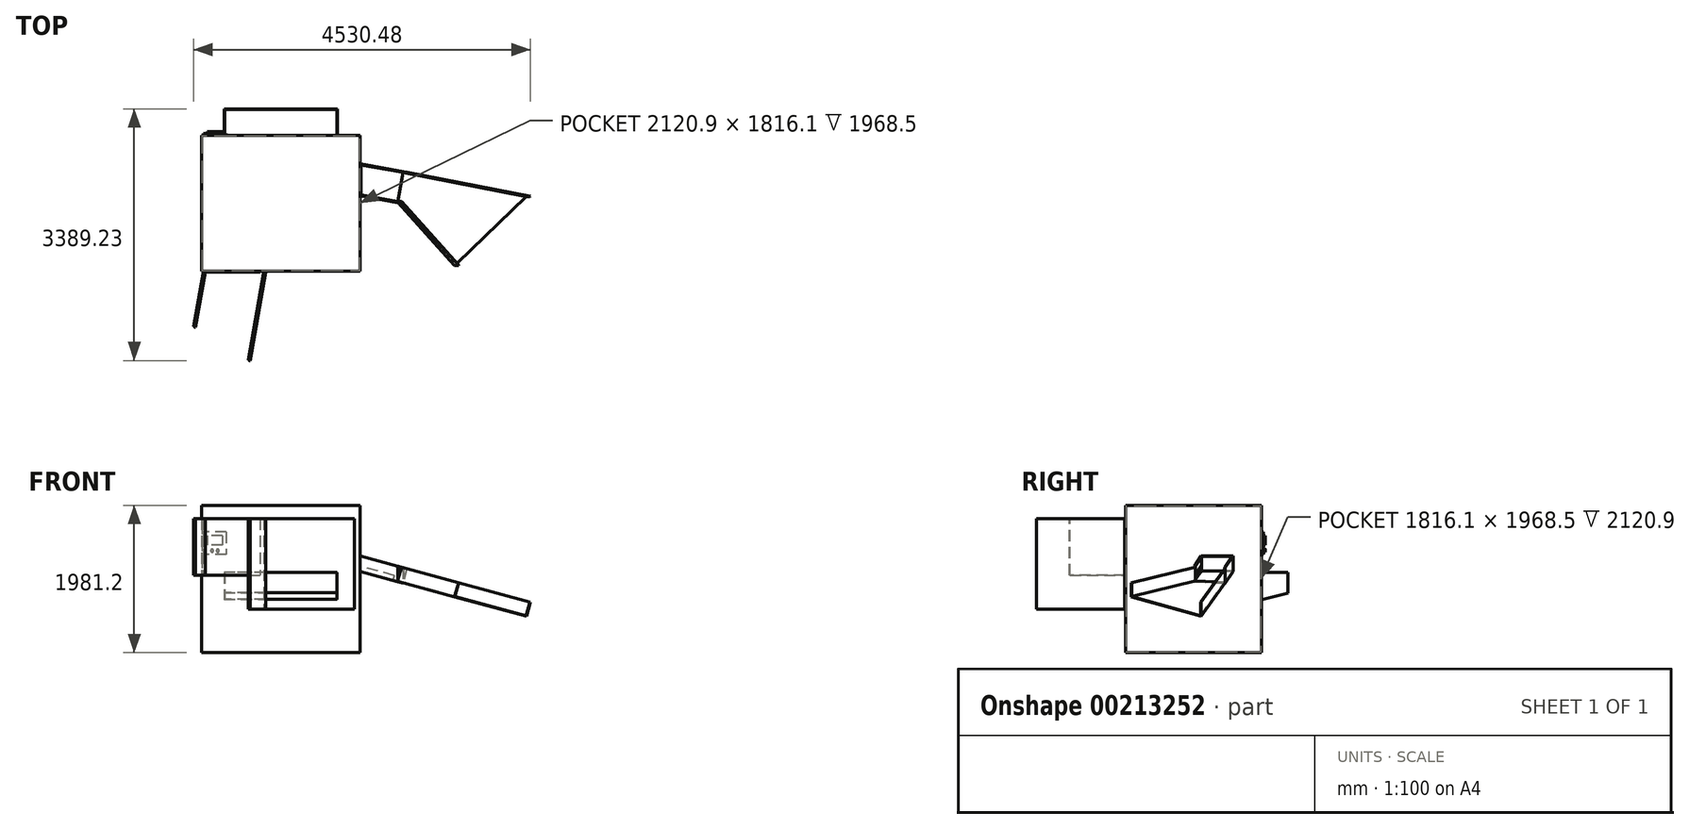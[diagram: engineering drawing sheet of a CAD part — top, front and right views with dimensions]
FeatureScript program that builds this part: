
annotation { "Feature Type Name" : "Feature", "Feature Type Description" : "" }
export const myFeature = defineFeature(function(context is Context, id is Id, definition is map)
    precondition{}
    {
        {
            var Q0;
            Q0=qCreatedBy(makeId("Top.planeOp"),FACE);
            var sketch = newSketch(context, id + "F0", { "sketchPlane" : qUnion([Q0])});
            skLineSegment(sketch, "E0", {"start": v(0, 1828.8) * mm, "end": v(304.8, 1828.8) * mm});
            skLineSegment(sketch, "E1", {"start": v(304.8, 1828.8) * mm, "end": v(304.8, 2184.4) * mm});
            skLineSegment(sketch, "E2", {"start": v(304.8, 2184.4) * mm, "end": v(1828.8, 2184.4) * mm});
            skLineSegment(sketch, "E3", {"start": v(1828.8, 2184.4) * mm, "end": v(1828.8, 1828.8) * mm});
            skLineSegment(sketch, "E4", {"start": v(1828.8, 1828.8) * mm, "end": v(2133.6, 1828.8) * mm});
            skLineSegment(sketch, "E5", {"start": v(2133.6, 1828.8) * mm, "end": v(2133.6, 0) * mm});
            skLineSegment(sketch, "E6", {"start": v(2133.6, 0) * mm, "end": v(0, 0) * mm});
            skLineSegment(sketch, "E7", {"start": v(0, 0) * mm, "end": v(0, 1828.8) * mm});
            skLineSegment(sketch, "E8", {"start": v(2133.6, 1828.8) * mm, "end": v(2133.6, 1447.8) * mm});
            skLineSegment(sketch, "E9", {"start": v(2133.6, 1447.8) * mm, "end": v(2717.8, 1341.28) * mm});
            skLineSegment(sketch, "E10", {"start": v(2717.8, 1341.28) * mm, "end": v(2641.6, 923.37) * mm});
            skLineSegment(sketch, "E11", {"start": v(2641.6, 923.37) * mm, "end": v(2133.6, 1016) * mm});
            skLineSegment(sketch, "E12", {"start": v(2133.6, 1016) * mm, "end": v(2133.6, 1447.8) * mm});
            skSolve(sketch);
        }
        {
            var Q0;
            Q0=makeQuery(id+"F0.imprint","IMPRINT",FACE,{"disambiguationData":[TD([[makeQuery(id+"F0.imprint","IMPRINT",EDGE,{"derivedFrom":sQuery(id+"F0.wireOp",EDGE,"E0")}),-1.0]])]});
            var Q1;
            Q1=makeQuery(id+"F0.imprint","IMPRINT",FACE,{"disambiguationData":[TD([[makeQuery(id+"F0.imprint","IMPRINT",EDGE,{"derivedFrom":sQuery(id+"F0.wireOp",EDGE,"E9")}),-1.0]])]});
            extrude(context, id + "F1", {"entities" : qUnion([Q0, Q1]), "depth" : 1981.2 * mm});
        }
        {
            var Q0;
            Q0=qCreatedBy(makeId("Front.planeOp"),FACE);
            var sketch = newSketch(context, id + "F2", { "sketchPlane" : qUnion([Q0])});
            skLineSegment(sketch, "E13", {"start": v(2133.6, 0) * mm, "end": v(2133.6, 1092.2) * mm});
            skLineSegment(sketch, "E14", {"start": v(2133.6, 1092.2) * mm, "end": v(2717.8, 932.33) * mm});
            skLineSegment(sketch, "E15", {"start": v(2717.8, 932.33) * mm, "end": v(2717.8, 0) * mm});
            skLineSegment(sketch, "E16", {"start": v(2717.8, 0) * mm, "end": v(2133.6, 0) * mm});
            skLineSegment(sketch, "E17", {"start": v(2133.6, 1981.2) * mm, "end": v(2717.8, 1981.2) * mm});
            skLineSegment(sketch, "E18", {"start": v(2717.8, 1981.2) * mm, "end": v(2717.8, 1143) * mm});
            skLineSegment(sketch, "E19", {"start": v(2717.8, 1143) * mm, "end": v(2133.6, 1302.87) * mm});
            skLineSegment(sketch, "E20", {"start": v(2133.6, 1302.87) * mm, "end": v(2133.6, 1981.2) * mm});
            skSolve(sketch);
        }
        {
            var Q0;
            Q0=makeQuery(id+"F2.imprint","IMPRINT",FACE,{"disambiguationData":[TD([[makeQuery(id+"F2.imprint","IMPRINT",EDGE,{"derivedFrom":sQuery(id+"F2.wireOp",EDGE,"E17")}),-1.0]])]});
            var Q1;
            Q1=makeQuery(id+"F2.imprint","IMPRINT",FACE,{"disambiguationData":[TD([[makeQuery(id+"F2.imprint","IMPRINT",EDGE,{"derivedFrom":sQuery(id+"F2.wireOp",EDGE,"E13")}),-1.0]])]});
            extrude(context, id + "F3", {"entities" : qUnion([Q0, Q1]), "operationType" : NewBodyOperationType.REMOVE, "endBound" : BoundingType.THROUGH_ALL, "oppositeDirection" : true, "depth" : 25.4 * mm});
        }
        {
            var Q0;
            Q0=makeQuery(id+"F1.opExtrude","SWEPT_FACE",FACE,{"disambiguationData":[OSD([sQuery(id+"F0.wireOp",EDGE,"E7")])]});
            var sketch = newSketch(context, id + "F4", { "sketchPlane" : qUnion([Q0])});
            skLineSegment(sketch, "E21", {"start": v(-1828.8, 0) * mm, "end": v(-2184.4, 0) * mm});
            skLineSegment(sketch, "E22", {"start": v(-2184.4, 0) * mm, "end": v(-2184.4, 800.1) * mm});
            skLineSegment(sketch, "E23", {"start": v(-2184.4, 800.1) * mm, "end": v(-1828.8, 711.2) * mm});
            skLineSegment(sketch, "E24", {"start": v(-1828.8, 711.2) * mm, "end": v(-1828.8, 0) * mm});
            skLineSegment(sketch, "E25", {"start": v(-1828.8, 1981.2) * mm, "end": v(-2184.4, 1981.2) * mm});
            skLineSegment(sketch, "E26", {"start": v(-2184.4, 1981.2) * mm, "end": v(-2184.4, 1079.5) * mm});
            skLineSegment(sketch, "E27", {"start": v(-2184.4, 1079.5) * mm, "end": v(-1828.8, 1079.5) * mm});
            skLineSegment(sketch, "E28", {"start": v(-1828.8, 1079.5) * mm, "end": v(-1828.8, 1981.2) * mm});
            skSolve(sketch);
        }
        {
            var Q0;
            Q0=makeQuery(id+"F4.imprint","IMPRINT",FACE,{"disambiguationData":[TD([[makeQuery(id+"F4.imprint","IMPRINT",EDGE,{"derivedFrom":sQuery(id+"F4.wireOp",EDGE,"E25")}),1.0]])]});
            var Q1;
            Q1=makeQuery(id+"F4.imprint","IMPRINT",FACE,{"disambiguationData":[TD([[makeQuery(id+"F4.imprint","IMPRINT",EDGE,{"derivedFrom":sQuery(id+"F4.wireOp",EDGE,"E21")}),-1.0]])]});
            extrude(context, id + "F5", {"entities" : qUnion([Q0, Q1]), "operationType" : NewBodyOperationType.REMOVE, "endBound" : BoundingType.THROUGH_ALL, "oppositeDirection" : true, "depth" : 25.4 * mm});
        }
        {
            var Q0;
            Q0=makeQuery(id+"F5.boolean.opBoolean","COPY",FACE,{"derivedFrom":makeQuery(id+"F5.opExtrude","SWEPT_FACE",FACE,{"disambiguationData":[OSD([sQuery(id+"F4.wireOp",EDGE,"E27")])]})});
            shell(context, id + "F6", {"entities" : qUnion([Q0]), "thickness" : 6.35 * mm});
        }
        {
            var Q0;
            Q0=makeQuery(id+"F3.boolean.opBoolean","COPY",FACE,{"derivedFrom":makeQuery(id+"F3.opExtrude","SWEPT_FACE",FACE,{"disambiguationData":[OSD([sQuery(id+"F2.wireOp",EDGE,"E19")])]})});
            var sketch = newSketch(context, id + "F7", { "sketchPlane" : qUnion([Q0])});
            skLineSegment(sketch, "E29.0", {"start": v(2230.56, 938.05) * mm, "end": v(2304.85, 1331) * mm});
            skLineSegment(sketch, "E29.1", {"start": v(1726.74, 1026.66) * mm, "end": v(2230.56, 938.05) * mm});
            skLineSegment(sketch, "E29.2", {"start": v(1726.74, 1432.67) * mm, "end": v(1726.74, 1026.66) * mm});
            skLineSegment(sketch, "E29.3", {"start": v(2304.85, 1331) * mm, "end": v(1726.74, 1432.67) * mm});
            skSolve(sketch);
        }
        {
            var Q0;
            Q0=makeQuery(id+"F7.imprint","IMPRINT",FACE,{"disambiguationData":[TD([[makeQuery(id+"F7.imprint","IMPRINT",EDGE,{"derivedFrom":sQuery(id+"F7.wireOp",EDGE,"E29.0")}),1.0]])]});
            extrude(context, id + "F8", {"entities" : qUnion([Q0]), "operationType" : NewBodyOperationType.REMOVE, "oppositeDirection" : true, "depth" : 196.85 * mm});
        }
        {
            var Q0;
            Q0=makeQuery(id+"F1.opExtrude","SWEPT_FACE",FACE,{"disambiguationData":[OSD([sQuery(id+"F0.wireOp",EDGE,"E10")])]});
            var sketch = newSketch(context, id + "F9", { "sketchPlane" : qUnion([Q0])});
            skLineSegment(sketch, "E30", {"start": v(1794.36, 1143.62) * mm, "end": v(1794.36, 945.67) * mm});
            skLineSegment(sketch, "E31", {"start": v(1794.36, 945.67) * mm, "end": v(1394.93, 965.27) * mm});
            skLineSegment(sketch, "E32", {"start": v(1394.93, 965.27) * mm, "end": v(1394.93, 1163.23) * mm});
            skLineSegment(sketch, "E33", {"start": v(1794.36, 1143.62) * mm, "end": v(1798.95, 1186.6) * mm});
            skLineSegment(sketch, "E34", {"start": v(1798.95, 1186.6) * mm, "end": v(1379.63, 1213.91) * mm});
            skLineSegment(sketch, "E35", {"start": v(1379.63, 1213.91) * mm, "end": v(1394.93, 1163.23) * mm});
            skSolve(sketch);
        }
        {
            var Q0;
            Q0=makeQuery(id+"F9.imprint","IMPRINT",FACE,{"disambiguationData":[TD([[makeQuery(id+"F9.imprint","IMPRINT",EDGE,{"derivedFrom":sQuery(id+"F9.wireOp",EDGE,"E30")}),-1.0]])]});
            var Q1;
            {var subQ0=sQuery(id+"F9.wireOp",EDGE,"E33");Q1=makeQuery(id+"F9.imprint","IMPRINT",FACE,{"disambiguationData":[TD([[makeQuery(id+"F9.imprint","IMPRINT",EDGE,{"derivedFrom":subQ0}),1.0]])]});}
            extrude(context, id + "F10", {"entities" : qUnion([Q0, Q1]), "operationType" : NewBodyOperationType.REMOVE, "oppositeDirection" : true, "depth" : 19.05 * mm});
        }
        {
            var Q0;
            Q0=makeQuery(id+"F1.opExtrude","SWEPT_FACE",FACE,{"disambiguationData":[OSD([sQuery(id+"F0.wireOp",EDGE,"E6")])]});
            var sketch = newSketch(context, id + "F11", { "sketchPlane" : qUnion([Q0])});
            skLineSegment(sketch, "E36.bottom", {"start": v(838.2, 1803.4) * mm, "end": v(2057.4, 1803.4) * mm});
            skLineSegment(sketch, "E36.top", {"start": v(838.2, 584.2) * mm, "end": v(2057.4, 584.2) * mm});
            skLineSegment(sketch, "E36.left", {"start": v(838.2, 1803.4) * mm, "end": v(838.2, 584.2) * mm});
            skLineSegment(sketch, "E36.right", {"start": v(2057.4, 1803.4) * mm, "end": v(2057.4, 584.2) * mm});
            skLineSegment(sketch, "E37.bottom", {"start": v(25.4, 1803.4) * mm, "end": v(787.4, 1803.4) * mm});
            skLineSegment(sketch, "E37.top", {"start": v(25.4, 1041.4) * mm, "end": v(787.4, 1041.4) * mm});
            skLineSegment(sketch, "E37.left", {"start": v(25.4, 1803.4) * mm, "end": v(25.4, 1041.4) * mm});
            skLineSegment(sketch, "E37.right", {"start": v(787.4, 1803.4) * mm, "end": v(787.4, 1041.4) * mm});
            skSolve(sketch);
        }
        {
            var Q0;
            Q0=makeQuery(id+"F11.imprint","IMPRINT",FACE,{"disambiguationData":[TD([[makeQuery(id+"F11.imprint","IMPRINT",EDGE,{"derivedFrom":sQuery(id+"F11.wireOp",EDGE,"E37.bottom")}),-1.0]])]});
            var Q1;
            Q1=makeQuery(id+"F11.imprint","IMPRINT",FACE,{"disambiguationData":[TD([[makeQuery(id+"F11.imprint","IMPRINT",EDGE,{"derivedFrom":sQuery(id+"F11.wireOp",EDGE,"E36.bottom")}),-1.0]])]});
            extrude(context, id + "F12", {"entities" : qUnion([Q0, Q1]), "operationType" : NewBodyOperationType.ADD, "depth" : 12.7 * mm});
        }
        {
            var Q0;
            Q0=makeQuery(id+"F12.opExtrude","SWEPT_FACE",FACE,{"disambiguationData":[OSD([sQuery(id+"F11.wireOp",EDGE,"E36.bottom")])]});
            var sketch = newSketch(context, id + "F13", { "sketchPlane" : qUnion([Q0])});
            skCircle(sketch, "E38", {"center": v(838.2, 0) * mm, "radius": 1219.2 * mm});
            skLineSegment(sketch, "E39", {"start": v(838.2, 0) * mm, "end": v(626.49, -1200.68) * mm});
            skLineSegment(sketch, "E40", {"start": v(626.49, -1200.68) * mm, "end": v(651.5, -1205.09) * mm});
            skLineSegment(sketch, "E41", {"start": v(651.5, -1205.09) * mm, "end": v(863.21, -4.41) * mm});
            skLineSegment(sketch, "E42", {"start": v(863.21, -4.41) * mm, "end": v(838.2, 0) * mm});
            skSolve(sketch);
        }
        {
            var Q0;
            {var subQ7=sQuery(id+"F13.wireOp",EDGE,"E39");Q0=makeQuery(id+"F13.imprint","IMPRINT",FACE,{"disambiguationData":[TD([[makeQuery(id+"F13.imprint","IMPRINT",EDGE,{"derivedFrom":subQ7}),1.0]])]});}
            var Q1;
            Q1=makeQuery(id+"F12.opExtrude","SWEPT_FACE",FACE,{"disambiguationData":[OSD([sQuery(id+"F11.wireOp",EDGE,"E36.top")])]});
            extrude(context, id + "F14", {"entities" : qUnion([Q0]), "operationType" : NewBodyOperationType.ADD, "endBound" : BoundingType.UP_TO_SURFACE, "oppositeDirection" : true, "endBoundEntityFace" : qUnion([Q1]), "depth" : 25.4 * mm});
        }
        {
            var Q0;
            Q0=makeQuery(id+"F12.opExtrude","CAP_FACE",FACE,{"disambiguationData":[OSD([sQuery(id+"F11.wireOp",EDGE,"E36.bottom"),sQuery(id+"F11.wireOp",EDGE,"E36.top"),sQuery(id+"F11.wireOp",EDGE,"E36.left"),sQuery(id+"F11.wireOp",EDGE,"E36.right")])],"isStart":false});
            extrude(context, id + "F15", {"entities" : qUnion([Q0]), "operationType" : NewBodyOperationType.REMOVE, "oppositeDirection" : true, "depth" : 25.4 * mm});
        }
        {
            var Q0;
            Q0=makeQuery(id+"F12.opExtrude","SWEPT_FACE",FACE,{"disambiguationData":[OSD([sQuery(id+"F11.wireOp",EDGE,"E37.bottom")])]});
            var sketch = newSketch(context, id + "F16", { "sketchPlane" : qUnion([Q0])});
            skCircle(sketch, "E43", {"center": v(25.4, 0) * mm, "radius": 762 * mm});
            skLineSegment(sketch, "E44", {"start": v(25.4, 0) * mm, "end": v(-106.92, -750.42) * mm});
            skLineSegment(sketch, "E45", {"start": v(-106.92, -750.42) * mm, "end": v(-81.9, -754.83) * mm});
            skLineSegment(sketch, "E46", {"start": v(-81.9, -754.83) * mm, "end": v(50.41, -4.41) * mm});
            skLineSegment(sketch, "E47", {"start": v(50.41, -4.41) * mm, "end": v(25.4, 0) * mm});
            skSolve(sketch);
        }
        {
            var Q0;
            {var subQ2=sQuery(id+"F16.wireOp",EDGE,"E44");Q0=makeQuery(id+"F16.imprint","IMPRINT",FACE,{"disambiguationData":[TD([[makeQuery(id+"F16.imprint","IMPRINT",EDGE,{"derivedFrom":subQ2}),1.0]])]});}
            var Q1;
            Q1=makeQuery(id+"F12.opExtrude","SWEPT_FACE",FACE,{"disambiguationData":[OSD([sQuery(id+"F11.wireOp",EDGE,"E37.top")])]});
            extrude(context, id + "F17", {"entities" : qUnion([Q0]), "operationType" : NewBodyOperationType.ADD, "endBound" : BoundingType.UP_TO_SURFACE, "oppositeDirection" : true, "endBoundEntityFace" : qUnion([Q1]), "depth" : 25.4 * mm});
        }
        {
            var Q0;
            Q0=makeQuery(id+"F5.boolean.opBoolean","MERGE",FACE,{"derivedFrom":[makeQuery(id+"F1.opExtrude","SWEPT_FACE",FACE,{"disambiguationData":[OSD([sQuery(id+"F0.wireOp",EDGE,"E0")])]}),makeQuery(id+"F1.opExtrude","SWEPT_FACE",FACE,{"disambiguationData":[OSD([sQuery(id+"F0.wireOp",EDGE,"E4")])]}),makeQuery(id+"F5.opExtrude","SWEPT_FACE",FACE,{"disambiguationData":[OSD([sQuery(id+"F4.wireOp",EDGE,"E24")])]}),makeQuery(id+"F5.opExtrude","SWEPT_FACE",FACE,{"disambiguationData":[OSD([sQuery(id+"F4.wireOp",EDGE,"E28")])]})]});
            var sketch = newSketch(context, id + "F18", { "sketchPlane" : qUnion([Q0])});
            skLineSegment(sketch, "E48.bottom", {"start": v(-330.2, 1625.6) * mm, "end": v(-25.4, 1625.6) * mm});
            skLineSegment(sketch, "E48.top", {"start": v(-330.2, 1320.8) * mm, "end": v(-25.4, 1320.8) * mm});
            skLineSegment(sketch, "E48.left", {"start": v(-330.2, 1625.6) * mm, "end": v(-330.2, 1320.8) * mm});
            skLineSegment(sketch, "E48.right", {"start": v(-25.4, 1625.6) * mm, "end": v(-25.4, 1320.8) * mm});
            skSolve(sketch);
        }
        {
            var Q0;
            Q0=makeQuery(id+"F18.imprint","IMPRINT",FACE,{"disambiguationData":[TD([[makeQuery(id+"F18.imprint","IMPRINT",EDGE,{"derivedFrom":sQuery(id+"F18.wireOp",EDGE,"E48.bottom")}),-1.0]])]});
            extrude(context, id + "F19", {"entities" : qUnion([Q0]), "operationType" : NewBodyOperationType.ADD, "depth" : 25.4 * mm});
        }
        {
            var Q0;
            Q0=makeQuery(id+"F19.opExtrude","CAP_FACE",FACE,{"disambiguationData":[OSD([sQuery(id+"F18.wireOp",EDGE,"E48.bottom"),sQuery(id+"F18.wireOp",EDGE,"E48.top"),sQuery(id+"F18.wireOp",EDGE,"E48.left"),sQuery(id+"F18.wireOp",EDGE,"E48.right")])],"isStart":false});
            var sketch = newSketch(context, id + "F20", { "sketchPlane" : qUnion([Q0])});
            skLineSegment(sketch, "E49.bottom", {"start": v(-279.4, 1574.8) * mm, "end": v(-76.2, 1574.8) * mm});
            skLineSegment(sketch, "E49.top", {"start": v(-279.4, 1447.8) * mm, "end": v(-76.2, 1447.8) * mm});
            skLineSegment(sketch, "E49.left", {"start": v(-279.4, 1574.8) * mm, "end": v(-279.4, 1447.8) * mm});
            skLineSegment(sketch, "E49.right", {"start": v(-76.2, 1574.8) * mm, "end": v(-76.2, 1447.8) * mm});
            skCircle(sketch, "E50", {"center": v(-215.9, 1371.6) * mm, "radius": 19.05 * mm});
            skCircle(sketch, "E51", {"center": v(-139.7, 1371.6) * mm, "radius": 19.05 * mm});
            skLineSegment(sketch, "E52", {"start": v(-215.9, 1371.6) * mm, "end": v(-139.7, 1371.6) * mm, "construction": true});
            skLineSegment(sketch, "E53", {"start": v(-177.8, 1371.6) * mm, "end": v(-177.8, 1625.6) * mm});
            skSolve(sketch);
        }
        {
            var Q0;
            {var subQ0=sQuery(id+"F20.wireOp",EDGE,"E49.left");Q0=makeQuery(id+"F20.imprint","IMPRINT",FACE,{"disambiguationData":[TD([[makeQuery(id+"F20.imprint","IMPRINT",EDGE,{"derivedFrom":subQ0}),1.0]])]});}
            var Q1;
            {var subQ0=sQuery(id+"F20.wireOp",EDGE,"E49.right");Q1=makeQuery(id+"F20.imprint","IMPRINT",FACE,{"disambiguationData":[TD([[makeQuery(id+"F20.imprint","IMPRINT",EDGE,{"derivedFrom":subQ0}),-1.0]])]});}
            var Q2;
            Q2=makeQuery(id+"F20.imprint","IMPRINT",FACE,{"disambiguationData":[TD([[makeQuery(id+"F20.imprint","IMPRINT",EDGE,{"derivedFrom":sQuery(id+"F20.wireOp",EDGE,"E50")}),1.0]])]});
            var Q3;
            Q3=makeQuery(id+"F20.imprint","IMPRINT",FACE,{"disambiguationData":[TD([[makeQuery(id+"F20.imprint","IMPRINT",EDGE,{"derivedFrom":sQuery(id+"F20.wireOp",EDGE,"E51")}),1.0]])]});
            extrude(context, id + "F21", {"entities" : qUnion([Q0, Q1, Q2, Q3]), "operationType" : NewBodyOperationType.ADD, "depth" : 25.4 * mm});
        }
        {
            var Q0;
            Q0=makeQuery(id+"F8.boolean.opBoolean","MERGE",FACE,{"derivedFrom":[makeQuery(id+"F6.opShell","OFFSET_FACE",FACE,{"disambiguationData":[OSD([sQuery(id+"F2.wireOp",EDGE,"E14")])]}),makeQuery(id+"F8.opExtrude","CAP_FACE",FACE,{"disambiguationData":[OSD([sQuery(id+"F7.wireOp",EDGE,"E29.0"),sQuery(id+"F7.wireOp",EDGE,"E29.1"),sQuery(id+"F7.wireOp",EDGE,"E29.2"),sQuery(id+"F7.wireOp",EDGE,"E29.3")])],"isStart":false})]});
            var sketch = newSketch(context, id + "F22", { "sketchPlane" : qUnion([Q0])});
            skLineSegment(sketch, "E54", {"start": v(2289.29, 930.76) * mm, "end": v(3086.51, 76.6) * mm});
            skLineSegment(sketch, "E55", {"start": v(3086.51, 76.6) * mm, "end": v(4088.2, 1011.5) * mm});
            skLineSegment(sketch, "E56", {"start": v(4088.2, 1011.5) * mm, "end": v(2365.93, 1336.17) * mm});
            skLineSegment(sketch, "E57", {"start": v(2365.93, 1336.17) * mm, "end": v(2289.29, 930.76) * mm});
            skSolve(sketch);
        }
        {
            var Q0;
            Q0=makeQuery(id+"F22.imprint","IMPRINT",FACE,{"disambiguationData":[TD([[makeQuery(id+"F22.imprint","IMPRINT",EDGE,{"derivedFrom":sQuery(id+"F22.wireOp",EDGE,"E54")}),1.0]])]});
            var Q1;
            Q1=makeQuery(id+"F3.boolean.opBoolean","COPY",FACE,{"derivedFrom":makeQuery(id+"F3.opExtrude","SWEPT_FACE",FACE,{"disambiguationData":[OSD([sQuery(id+"F2.wireOp",EDGE,"E19")])]})});
            extrude(context, id + "F23", {"entities" : qUnion([Q0]), "endBound" : BoundingType.UP_TO_SURFACE, "endBoundEntityFace" : qUnion([Q1]), "depth" : 25.4 * mm});
        }
        {
            var Q0;
            Q0=makeQuery(id+"F23.opExtrude","CAP_FACE",FACE,{"disambiguationData":[OSD([sQuery(id+"F22.wireOp",EDGE,"E54"),sQuery(id+"F22.wireOp",EDGE,"E55"),sQuery(id+"F22.wireOp",EDGE,"E56"),sQuery(id+"F22.wireOp",EDGE,"E57")])],"isStart":false});
            var Q1;
            Q1=makeQuery(id+"F23.opExtrude","SWEPT_FACE",FACE,{"disambiguationData":[OSD([sQuery(id+"F22.wireOp",EDGE,"E55")])]});
            var Q2;
            Q2=makeQuery(id+"F23.opExtrude","SWEPT_FACE",FACE,{"disambiguationData":[OSD([sQuery(id+"F22.wireOp",EDGE,"E57")])]});
            shell(context, id + "F24", {"entities" : qUnion([Q0, Q1, Q2]), "thickness" : 6.35 * mm});
        }
    });
